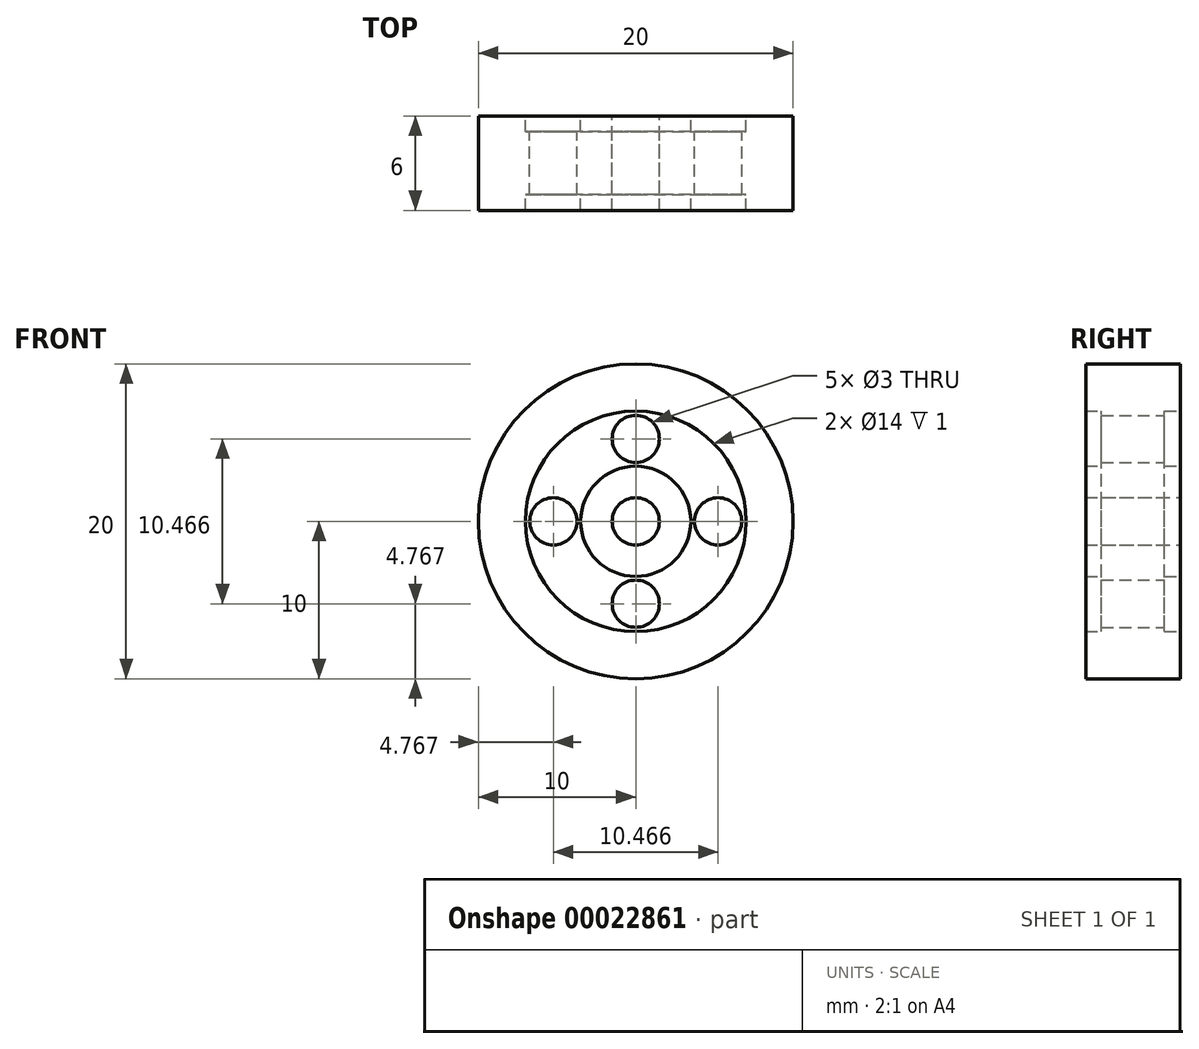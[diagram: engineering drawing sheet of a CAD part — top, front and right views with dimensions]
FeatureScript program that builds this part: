
annotation { "Feature Type Name" : "Feature", "Feature Type Description" : "" }
export const myFeature = defineFeature(function(context is Context, id is Id, definition is map)
    precondition{}
    {
        {
            var Q0;
            Q0=qCreatedBy(makeId("Front.planeOp"),FACE);
            var sketch = newSketch(context, id + "F0", { "sketchPlane" : qUnion([Q0])});
            skCircle(sketch, "E0", {"center": v(0, 0) * mm, "radius": 7 * mm});
            skCircle(sketch, "E1", {"center": v(0, 0) * mm, "radius": 1.5 * mm});
            skCircle(sketch, "E2", {"center": v(0, 5.23) * mm, "radius": 1.5 * mm});
            skCircle(sketch, "E3", {"center": v(0, 0) * mm, "radius": 10 * mm});
            skCircle(sketch, "E4", {"center": v(0, 0) * mm, "radius": 3.5 * mm});
            skCircle(sketch, "E5.1.0", {"center": v(-5.23, 0) * mm, "radius": 1.5 * mm});
            skCircle(sketch, "E5.2.0", {"center": v(0, -5.23) * mm, "radius": 1.5 * mm});
            skCircle(sketch, "E5.3.0", {"center": v(5.23, 0) * mm, "radius": 1.5 * mm});
            skSolve(sketch);
        }
        {
            var Q0;
            Q0=makeQuery(id+"F0.imprint","IMPRINT",FACE,{"disambiguationData":[TD([[makeQuery(id+"F0.imprint","IMPRINT",EDGE,{"derivedFrom":sQuery(id+"F0.wireOp",EDGE,"E0")}),-1.0]])]});
            extrude(context, id + "F1", {"entities" : qUnion([Q0]), "endBound" : BoundingType.SYMMETRIC, "depth" : 6 * mm});
        }
        {
            var Q0;
            Q0=makeQuery(id+"F0.imprint","IMPRINT",FACE,{"disambiguationData":[TD([[makeQuery(id+"F0.imprint","IMPRINT",EDGE,{"derivedFrom":sQuery(id+"F0.wireOp",EDGE,"E0")}),1.0]])]});
            extrude(context, id + "F2", {"entities" : qUnion([Q0]), "operationType" : NewBodyOperationType.ADD, "endBound" : BoundingType.SYMMETRIC, "depth" : 4 * mm});
        }
        {
            var Q0;
            Q0=makeQuery(id+"F0.imprint","IMPRINT",FACE,{"disambiguationData":[TD([[makeQuery(id+"F0.imprint","IMPRINT",EDGE,{"derivedFrom":sQuery(id+"F0.wireOp",EDGE,"E1")}),-1.0]])]});
            extrude(context, id + "F3", {"entities" : qUnion([Q0]), "operationType" : NewBodyOperationType.ADD, "endBound" : BoundingType.SYMMETRIC, "depth" : 6 * mm});
        }
    });
